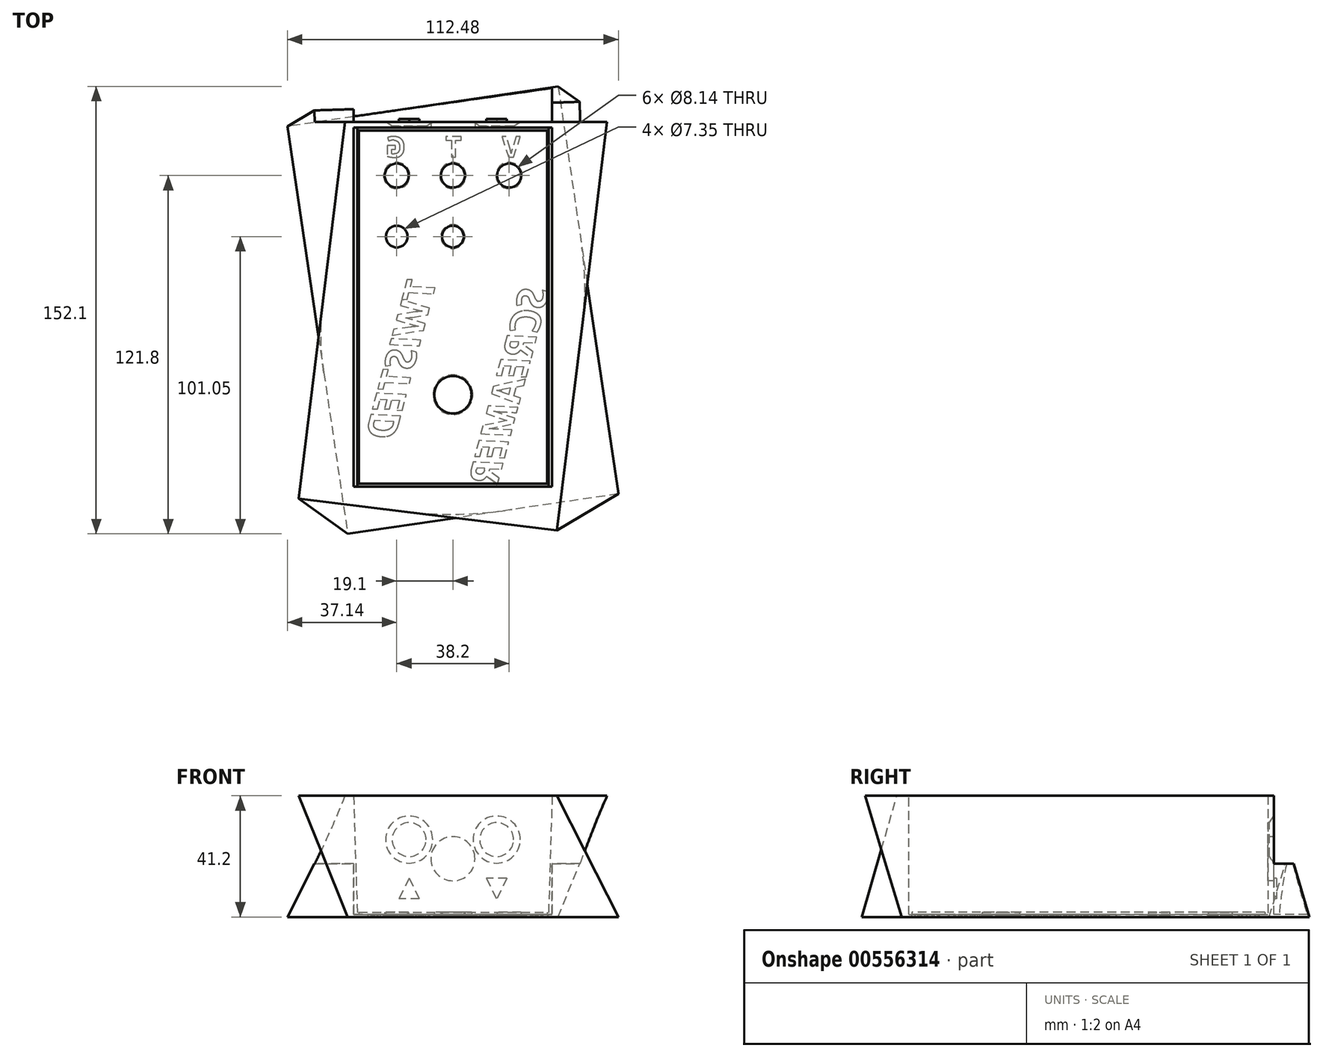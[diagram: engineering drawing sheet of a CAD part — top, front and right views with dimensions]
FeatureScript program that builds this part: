
annotation { "Feature Type Name" : "Feature", "Feature Type Description" : "" }
export const myFeature = defineFeature(function(context is Context, id is Id, definition is map)
    precondition{}
    {
        {
            var Q0;
            Q0=qCreatedBy(makeId("Top.planeOp"),FACE);
            var sketch = newSketch(context, id + "F0", { "sketchPlane" : qUnion([Q0])});
            skLineSegment(sketch, "E0.bottom", {"start": v(-36.5, 64) * mm, "end": v(36.5, 64) * mm});
            skLineSegment(sketch, "E0.top", {"start": v(-36.5, -64) * mm, "end": v(36.5, -64) * mm});
            skLineSegment(sketch, "E0.left", {"start": v(-36.5, 64) * mm, "end": v(-36.5, -64) * mm});
            skLineSegment(sketch, "E0.right", {"start": v(36.5, 64) * mm, "end": v(36.5, -64) * mm});
            skSolve(sketch);
        }
        {
            var Q0;
            Q0=makeQuery(id+"F0.imprint","IMPRINT",FACE,{"disambiguationData":[TD([[makeQuery(id+"F0.imprint","IMPRINT",EDGE,{"derivedFrom":sQuery(id+"F0.wireOp",EDGE,"E0.bottom")}),-1.0]])]});
            extrude(context, id + "F1", {"entities" : qUnion([Q0]), "depth" : 41.2 * mm, "offsetDistance" : 25 * mm});
        }
        {
            var Q0;
            {var subQ0=sQuery(id+"F0.wireOp",EDGE,"E0.bottom");var subQ1=sQuery(id+"F0.wireOp",EDGE,"E0.left");var subQ2=sQuery(id+"F0.wireOp",EDGE,"E0.top");var subQ3=sQuery(id+"F0.wireOp",EDGE,"E0.right");Q0=makeQuery(id+"F16.boolean.opBoolean","SPLIT",FACE,{"disambiguationData":[TD([makeQuery(id+"F1.opExtrude","SWEPT_FACE",FACE,{"disambiguationData":[OSD([subQ0])]})])],"derivedFrom":makeQuery(id+"F1.opExtrude","CAP_FACE",FACE,{"disambiguationData":[OSD([subQ0,subQ2,subQ1,subQ3])],"isStart":true})});}
            var sketch = newSketch(context, id + "F2", { "sketchPlane" : qUnion([Q0])});
            skLineSegment(sketch, "E1.bottom", {"start": v(35.76, -75.05) * mm, "end": v(-56.24, -61.45) * mm});
            skLineSegment(sketch, "E1.top", {"start": v(56.24, 63.45) * mm, "end": v(-35.76, 77.05) * mm});
            skLineSegment(sketch, "E1.left", {"start": v(35.76, -75.05) * mm, "end": v(56.24, 63.45) * mm});
            skLineSegment(sketch, "E1.right", {"start": v(-56.24, -61.45) * mm, "end": v(-35.76, 77.05) * mm});
            skPoint(sketch, "E1.middle", {"position": v(0, 1) * mm});
            skSolve(sketch);
        }
        {
            var Q0;
            Q0=makeQuery(id+"F1.opExtrude","CAP_FACE",FACE,{"disambiguationData":[OSD([sQuery(id+"F0.wireOp",EDGE,"E0.bottom"),sQuery(id+"F0.wireOp",EDGE,"E0.top"),sQuery(id+"F0.wireOp",EDGE,"E0.left"),sQuery(id+"F0.wireOp",EDGE,"E0.right")])],"isStart":false});
            var sketch = newSketch(context, id + "F3", { "sketchPlane" : qUnion([Q0])});
            skLineSegment(sketch, "E2.bottom", {"start": v(-35.35, 73.87) * mm, "end": v(52.41, 63.1) * mm});
            skLineSegment(sketch, "E2.top", {"start": v(-52.41, -65.1) * mm, "end": v(35.35, -75.87) * mm});
            skLineSegment(sketch, "E2.left", {"start": v(-35.35, 73.87) * mm, "end": v(-52.41, -65.1) * mm});
            skLineSegment(sketch, "E2.right", {"start": v(52.41, 63.1) * mm, "end": v(35.35, -75.87) * mm});
            skPoint(sketch, "E2.middle", {"position": v(0, -1) * mm});
            skSolve(sketch);
        }
        {
            var Q1;
            Q1=qSketchRegion(id+"F2",true);
            var Q2;
            Q2=qSketchRegion(id+"F3",true);
            var Q3;
            Q3=sQuery(id+"F2.wireOp",VERTEX,"E1.left.start");
            var Q4;
            Q4=sQuery(id+"F3.wireOp",VERTEX,"E2.right.start");
            loft(context, id + "F4", {"operationType" : NewBodyOperationType.ADD, "sheetProfilesArray" : [{ "sheetProfileEntities" : qUnion([Q1]) }, { "sheetProfileEntities" : qUnion([Q2]) }], "matchConnections" : true, "connections" : [{ "connectionEntities" : qUnion([Q3, Q4]), "connectionEdgeQueries" : qUnion([]), "connectionEdgeParameters" : [] }]});
        }
        {
            var Q0;
            Q0=makeQuery(id+"F1.opExtrude","CAP_FACE",FACE,{"disambiguationData":[OSD([sQuery(id+"F0.wireOp",EDGE,"E0.bottom"),sQuery(id+"F0.wireOp",EDGE,"E0.top"),sQuery(id+"F0.wireOp",EDGE,"E0.left"),sQuery(id+"F0.wireOp",EDGE,"E0.right")])],"isStart":false});
            var sketch = newSketch(context, id + "F5", { "sketchPlane" : qUnion([Q0])});
            skLineSegment(sketch, "E3.bottom", {"start": v(-33.75, 61) * mm, "end": v(33.75, 61) * mm});
            skLineSegment(sketch, "E3.top", {"start": v(-33.75, -61) * mm, "end": v(33.75, -61) * mm});
            skLineSegment(sketch, "E3.left", {"start": v(-33.75, 61) * mm, "end": v(-33.75, -61) * mm});
            skLineSegment(sketch, "E3.right", {"start": v(33.75, 61) * mm, "end": v(33.75, -61) * mm});
            skSolve(sketch);
        }
        {
            var Q0;
            Q0=makeQuery(id+"F5.imprint","IMPRINT",FACE,{"disambiguationData":[TD([[makeQuery(id+"F5.imprint","IMPRINT",EDGE,{"derivedFrom":sQuery(id+"F5.wireOp",EDGE,"E3.bottom")}),-1.0]])]});
            extrude(context, id + "F6", {"entities" : qUnion([Q0]), "operationType" : NewBodyOperationType.REMOVE, "oppositeDirection" : true, "depth" : 40.4 * mm, "offsetDistance" : 25 * mm});
        }
        {
            var Q0;
            Q0=makeQuery(id+"F6.boolean.opBoolean","COPY",FACE,{"derivedFrom":makeQuery(id+"F6.opExtrude","CAP_FACE",FACE,{"disambiguationData":[OSD([sQuery(id+"F5.wireOp",EDGE,"E3.bottom"),sQuery(id+"F5.wireOp",EDGE,"E3.top"),sQuery(id+"F5.wireOp",EDGE,"E3.left"),sQuery(id+"F5.wireOp",EDGE,"E3.right")])],"isStart":false})});
            var sketch = newSketch(context, id + "F7", { "sketchPlane" : qUnion([Q0])});
            skCircle(sketch, "E4", {"center": v(-19.1, 44.75) * mm, "radius": 4.07 * mm});
            skCircle(sketch, "E5", {"center": v(0, 44.75) * mm, "radius": 4.07 * mm});
            skCircle(sketch, "E6", {"center": v(19.1, 44.75) * mm, "radius": 4.07 * mm});
            skCircle(sketch, "E7", {"center": v(0, -29.75) * mm, "radius": 6.35 * mm});
            skLineSegment(sketch, "E8", {"start": v(19.1, 44.75) * mm, "end": v(0, 44.75) * mm, "construction": true});
            skCircle(sketch, "E9", {"center": v(0, 24) * mm, "radius": 3.67 * mm});
            skCircle(sketch, "E10", {"center": v(-19.1, 24) * mm, "radius": 3.67 * mm});
            skSolve(sketch);
        }
        {
            var Q0;
            Q0=qSketchRegion(id+"F7",true);
            extrude(context, id + "F8", {"entities" : qUnion([Q0]), "operationType" : NewBodyOperationType.REMOVE, "oppositeDirection" : true, "depth" : 25 * mm, "offsetDistance" : 25 * mm});
        }
        {
            var Q0;
            Q0=makeQuery(id+"F6.boolean.opBoolean","COPY",FACE,{"derivedFrom":makeQuery(id+"F6.opExtrude","SWEPT_FACE",FACE,{"disambiguationData":[OSD([sQuery(id+"F5.wireOp",EDGE,"E3.bottom")])]})});
            cPlane(context, id + "F9", {"entities" : qUnion([Q0]), "cplaneType" : CPlaneType.OFFSET, "offset" : 2 * mm, "oppositeDirection" : true, "width" : 150 * mm, "height" : 150 * mm});
        }
        {
            var Q0;
            Q0=qCreatedBy(id+"F9.planeOp",FACE);
            var sketch = newSketch(context, id + "F10", { "sketchPlane" : qUnion([Q0])});
            skCircle(sketch, "E11", {"center": v(0, 19.8) * mm, "radius": 7.5 * mm});
            skCircle(sketch, "E12", {"center": v(14.87, 26.3) * mm, "radius": 5.76 * mm});
            skCircle(sketch, "E13", {"center": v(-14.88, 26.3) * mm, "radius": 5.76 * mm});
            skSolve(sketch);
        }
        {
            var Q0;
            Q0=qSketchRegion(id+"F10",true);
            extrude(context, id + "F11", {"entities" : qUnion([Q0]), "operationType" : NewBodyOperationType.REMOVE, "endBound" : BoundingType.SYMMETRIC, "oppositeDirection" : true, "depth" : 30 * mm, "offsetDistance" : 25 * mm});
        }
        {
            var Q0;
            Q0=qCreatedBy(id+"F9.planeOp",FACE);
            var sketch = newSketch(context, id + "F12", { "sketchPlane" : qUnion([Q0])});
            skLineSegment(sketch, "E14.0", {"start": v(-33.75, 0.8) * mm, "end": v(-33.75, 41.2) * mm});
            skLineSegment(sketch, "E15.0", {"start": v(-33.75, 0.8) * mm, "end": v(33.75, 0.8) * mm});
            skLineSegment(sketch, "E16.0", {"start": v(33.75, 0.8) * mm, "end": v(33.75, 41.2) * mm});
            skLineSegment(sketch, "E17.0", {"start": v(-33.75, 41.2) * mm, "end": v(33.75, 41.2) * mm});
            skSolve(sketch);
        }
        {
            var Q0;
            Q0=qSketchRegion(id+"F12",true);
            extrude(context, id + "F13", {"entities" : qUnion([Q0]), "operationType" : NewBodyOperationType.REMOVE, "oppositeDirection" : true, "depth" : 25 * mm, "offsetDistance" : 25 * mm});
        }
        {
            var Q0;
            Q0=qCreatedBy(makeId("Front.planeOp"),FACE);
            cPlane(context, id + "F14", {"entities" : qUnion([Q0]), "cplaneType" : CPlaneType.OFFSET, "offset" : 38 * mm, "width" : 150 * mm, "height" : 150 * mm});
        }
        {
            var Q0;
            Q0=makeQuery(id+"F1.opExtrude","CAP_FACE",FACE,{"disambiguationData":[OSD([sQuery(id+"F0.wireOp",EDGE,"E0.bottom"),sQuery(id+"F0.wireOp",EDGE,"E0.top"),sQuery(id+"F0.wireOp",EDGE,"E0.left"),sQuery(id+"F0.wireOp",EDGE,"E0.right")])],"isStart":true});
            var sketch = newSketch(context, id + "F15", { "sketchPlane" : qUnion([Q0])});
            skText(sketch, "E18", { "text": "V", "fontName": "OpenSans-Bold.ttf"});
            skText(sketch, "E19", { "text": "T", "fontName": "OpenSans-Bold.ttf"});
            skText(sketch, "E20", { "text": "G", "fontName": "OpenSans-Bold.ttf"});
            const initialGuessF15  = {"E18": [0.02295, -0.051, -1, 0, 0.007], "E19": [0.00303, -0.051, -1, 0, 0.007], "E20": [-0.016, -0.051, -1, 0, 0.007]};
            skSetInitialGuess(sketch, initialGuessF15);
            skSolve(sketch);
        }
        {
            var Q0;
            Q0=qSketchRegion(id+"F15",true);
            extrude(context, id + "F16", {"entities" : qUnion([Q0]), "operationType" : NewBodyOperationType.REMOVE, "endBound" : BoundingType.THROUGH_ALL, "oppositeDirection" : true, "depth" : 0.5 * mm, "offsetDistance" : 25 * mm});
        }
        {
            var Q0;
            Q0=makeQuery(id+"F13.boolean.opBoolean","COPY",FACE,{"derivedFrom":makeQuery(id+"F13.opExtrude","CAP_FACE",FACE,{"disambiguationData":[OSD([sQuery(id+"F12.wireOp",EDGE,"E14.0"),sQuery(id+"F12.wireOp",EDGE,"E15.0"),sQuery(id+"F12.wireOp",EDGE,"E16.0"),sQuery(id+"F12.wireOp",EDGE,"E17.0")])],"isStart":true})});
            var sketch = newSketch(context, id + "F17", { "sketchPlane" : qUnion([Q0])});
            skLineSegment(sketch, "E21", {"start": v(75, 18.06) * mm, "end": v(-75, 18.06) * mm});
            skLineSegment(sketch, "E22", {"start": v(-75, 18.06) * mm, "end": v(-75, 44.5) * mm});
            skLineSegment(sketch, "E23", {"start": v(-75, 44.5) * mm, "end": v(75, 44.5) * mm});
            skLineSegment(sketch, "E24", {"start": v(75, 44.5) * mm, "end": v(75, 18.06) * mm});
            skSolve(sketch);
        }
        {
            var Q0;
            Q0=qSketchRegion(id+"F17",true);
            extrude(context, id + "F18", {"entities" : qUnion([Q0]), "operationType" : NewBodyOperationType.REMOVE, "depth" : 15 * mm, "offsetDistance" : 25 * mm});
        }
        {
            var Q0;
            Q0=makeQuery(id+"F13.boolean.opBoolean","INTERSECT",EDGE,{"derivedFrom":[makeQuery(id+"F11.boolean.opBoolean","COPY",FACE,{"derivedFrom":makeQuery(id+"F11.opExtrude","SWEPT_FACE",FACE,{"disambiguationData":[OSD([sQuery(id+"F10.wireOp",EDGE,"E13")])]})}),makeQuery(id+"F13.opExtrude","CAP_FACE",FACE,{"disambiguationData":[OSD([sQuery(id+"F12.wireOp",EDGE,"E14.0"),sQuery(id+"F12.wireOp",EDGE,"E15.0"),sQuery(id+"F12.wireOp",EDGE,"E16.0"),sQuery(id+"F12.wireOp",EDGE,"E17.0")])],"isStart":true})]});
            var Q1;
            Q1=makeQuery(id+"F13.boolean.opBoolean","INTERSECT",EDGE,{"derivedFrom":[makeQuery(id+"F11.boolean.opBoolean","COPY",FACE,{"derivedFrom":makeQuery(id+"F11.opExtrude","SWEPT_FACE",FACE,{"disambiguationData":[OSD([sQuery(id+"F10.wireOp",EDGE,"E12")])]})}),makeQuery(id+"F13.opExtrude","CAP_FACE",FACE,{"disambiguationData":[OSD([sQuery(id+"F12.wireOp",EDGE,"E14.0"),sQuery(id+"F12.wireOp",EDGE,"E15.0"),sQuery(id+"F12.wireOp",EDGE,"E16.0"),sQuery(id+"F12.wireOp",EDGE,"E17.0")])],"isStart":true})]});
            chamfer(context, id + "F19", {"entities" : qUnion([Q0, Q1]), "chamferType" : ChamferType.TWO_OFFSETS, "width1" : 1.5 * mm, "oppositeDirection" : false, "width2" : 2.25 * mm, "tangentPropagation" : true});
        }
        {
            var Q0;
            {var subQ0=sQuery(id+"F0.wireOp",EDGE,"E0.bottom");var subQ1=sQuery(id+"F0.wireOp",EDGE,"E0.top");var subQ2=sQuery(id+"F0.wireOp",EDGE,"E0.left");var subQ3=sQuery(id+"F0.wireOp",EDGE,"E0.right");Q0=makeQuery(id+"F8.boolean.opBoolean","INTERSECT",EDGE,{"derivedFrom":[makeQuery(id+"F4.boolean.opBoolean","MERGE",FACE,{"derivedFrom":[makeQuery(id+"F1.opExtrude","CAP_FACE",FACE,{"disambiguationData":[OSD([subQ0,subQ1,subQ2,subQ3])],"isStart":true}),makeQuery(id+"F4.opLoft","CAP_FACE",FACE,{"disambiguationData":[OSD([makeQuery(id+"F2.imprint","IMPRINT",FACE,{"disambiguationData":[TD([[makeQuery(id+"F2.imprint","IMPRINT",EDGE,{"derivedFrom":makeQuery(id+"F1.opExtrude","CAP_EDGE",EDGE,{"disambiguationData":[OSD([subQ0])],"isStart":true})}),1.0]])]})])],"isStart":true})]}),makeQuery(id+"F8.opExtrude","SWEPT_FACE",FACE,{"disambiguationData":[OSD([sQuery(id+"F7.wireOp",EDGE,"E6")])]})]});}
            var Q1;
            {var subQ0=sQuery(id+"F0.wireOp",EDGE,"E0.bottom");var subQ1=sQuery(id+"F0.wireOp",EDGE,"E0.top");var subQ2=sQuery(id+"F0.wireOp",EDGE,"E0.left");var subQ3=sQuery(id+"F0.wireOp",EDGE,"E0.right");Q1=makeQuery(id+"F8.boolean.opBoolean","INTERSECT",EDGE,{"derivedFrom":[makeQuery(id+"F4.boolean.opBoolean","MERGE",FACE,{"derivedFrom":[makeQuery(id+"F1.opExtrude","CAP_FACE",FACE,{"disambiguationData":[OSD([subQ0,subQ1,subQ2,subQ3])],"isStart":true}),makeQuery(id+"F4.opLoft","CAP_FACE",FACE,{"disambiguationData":[OSD([makeQuery(id+"F2.imprint","IMPRINT",FACE,{"disambiguationData":[TD([[makeQuery(id+"F2.imprint","IMPRINT",EDGE,{"derivedFrom":makeQuery(id+"F1.opExtrude","CAP_EDGE",EDGE,{"disambiguationData":[OSD([subQ0])],"isStart":true})}),1.0]])]})])],"isStart":true})]}),makeQuery(id+"F8.opExtrude","SWEPT_FACE",FACE,{"disambiguationData":[OSD([sQuery(id+"F7.wireOp",EDGE,"E5")])]})]});}
            var Q2;
            {var subQ0=sQuery(id+"F0.wireOp",EDGE,"E0.bottom");var subQ1=sQuery(id+"F0.wireOp",EDGE,"E0.top");var subQ2=sQuery(id+"F0.wireOp",EDGE,"E0.left");var subQ3=sQuery(id+"F0.wireOp",EDGE,"E0.right");Q2=makeQuery(id+"F8.boolean.opBoolean","INTERSECT",EDGE,{"derivedFrom":[makeQuery(id+"F4.boolean.opBoolean","MERGE",FACE,{"derivedFrom":[makeQuery(id+"F1.opExtrude","CAP_FACE",FACE,{"disambiguationData":[OSD([subQ0,subQ1,subQ2,subQ3])],"isStart":true}),makeQuery(id+"F4.opLoft","CAP_FACE",FACE,{"disambiguationData":[OSD([makeQuery(id+"F2.imprint","IMPRINT",FACE,{"disambiguationData":[TD([[makeQuery(id+"F2.imprint","IMPRINT",EDGE,{"derivedFrom":makeQuery(id+"F1.opExtrude","CAP_EDGE",EDGE,{"disambiguationData":[OSD([subQ0])],"isStart":true})}),1.0]])]})])],"isStart":true})]}),makeQuery(id+"F8.opExtrude","SWEPT_FACE",FACE,{"disambiguationData":[OSD([sQuery(id+"F7.wireOp",EDGE,"E4")])]})]});}
            var Q3;
            {var subQ0=sQuery(id+"F0.wireOp",EDGE,"E0.bottom");var subQ1=sQuery(id+"F0.wireOp",EDGE,"E0.top");var subQ2=sQuery(id+"F0.wireOp",EDGE,"E0.left");var subQ3=sQuery(id+"F0.wireOp",EDGE,"E0.right");Q3=makeQuery(id+"F8.boolean.opBoolean","INTERSECT",EDGE,{"derivedFrom":[makeQuery(id+"F4.boolean.opBoolean","MERGE",FACE,{"derivedFrom":[makeQuery(id+"F1.opExtrude","CAP_FACE",FACE,{"disambiguationData":[OSD([subQ0,subQ1,subQ2,subQ3])],"isStart":true}),makeQuery(id+"F4.opLoft","CAP_FACE",FACE,{"disambiguationData":[OSD([makeQuery(id+"F2.imprint","IMPRINT",FACE,{"disambiguationData":[TD([[makeQuery(id+"F2.imprint","IMPRINT",EDGE,{"derivedFrom":makeQuery(id+"F1.opExtrude","CAP_EDGE",EDGE,{"disambiguationData":[OSD([subQ0])],"isStart":true})}),1.0]])]})])],"isStart":true})]}),makeQuery(id+"F8.opExtrude","SWEPT_FACE",FACE,{"disambiguationData":[OSD([sQuery(id+"F7.wireOp",EDGE,"E9")])]})]});}
            var Q4;
            {var subQ0=sQuery(id+"F0.wireOp",EDGE,"E0.bottom");var subQ1=sQuery(id+"F0.wireOp",EDGE,"E0.top");var subQ2=sQuery(id+"F0.wireOp",EDGE,"E0.left");var subQ3=sQuery(id+"F0.wireOp",EDGE,"E0.right");Q4=makeQuery(id+"F8.boolean.opBoolean","INTERSECT",EDGE,{"derivedFrom":[makeQuery(id+"F4.boolean.opBoolean","MERGE",FACE,{"derivedFrom":[makeQuery(id+"F1.opExtrude","CAP_FACE",FACE,{"disambiguationData":[OSD([subQ0,subQ1,subQ2,subQ3])],"isStart":true}),makeQuery(id+"F4.opLoft","CAP_FACE",FACE,{"disambiguationData":[OSD([makeQuery(id+"F2.imprint","IMPRINT",FACE,{"disambiguationData":[TD([[makeQuery(id+"F2.imprint","IMPRINT",EDGE,{"derivedFrom":makeQuery(id+"F1.opExtrude","CAP_EDGE",EDGE,{"disambiguationData":[OSD([subQ0])],"isStart":true})}),1.0]])]})])],"isStart":true})]}),makeQuery(id+"F8.opExtrude","SWEPT_FACE",FACE,{"disambiguationData":[OSD([sQuery(id+"F7.wireOp",EDGE,"KNiFqmuv-MMCi-B5FO-T3GH-z67XstVQp584")])]})]});}
            var Q5;
            {var subQ0=sQuery(id+"F0.wireOp",EDGE,"E0.bottom");var subQ1=sQuery(id+"F0.wireOp",EDGE,"E0.top");var subQ2=sQuery(id+"F0.wireOp",EDGE,"E0.left");var subQ3=sQuery(id+"F0.wireOp",EDGE,"E0.right");Q5=makeQuery(id+"F8.boolean.opBoolean","INTERSECT",EDGE,{"derivedFrom":[makeQuery(id+"F4.boolean.opBoolean","MERGE",FACE,{"derivedFrom":[makeQuery(id+"F1.opExtrude","CAP_FACE",FACE,{"disambiguationData":[OSD([subQ0,subQ1,subQ2,subQ3])],"isStart":true}),makeQuery(id+"F4.opLoft","CAP_FACE",FACE,{"disambiguationData":[OSD([makeQuery(id+"F2.imprint","IMPRINT",FACE,{"disambiguationData":[TD([[makeQuery(id+"F2.imprint","IMPRINT",EDGE,{"derivedFrom":makeQuery(id+"F1.opExtrude","CAP_EDGE",EDGE,{"disambiguationData":[OSD([subQ0])],"isStart":true})}),1.0]])]})])],"isStart":true})]}),makeQuery(id+"F8.opExtrude","SWEPT_FACE",FACE,{"disambiguationData":[OSD([sQuery(id+"F7.wireOp",EDGE,"E7")])]})]});}
            chamfer(context, id + "F20", {"entities" : qUnion([Q0, Q1, Q2, Q3, Q4, Q5]), "width" : 0.4 * mm, "tangentPropagation" : true});
        }
        {
            var Q0;
            {var subQ0=sQuery(id+"F0.wireOp",EDGE,"E0.bottom");var subQ1=sQuery(id+"F0.wireOp",EDGE,"E0.top");var subQ2=sQuery(id+"F0.wireOp",EDGE,"E0.left");var subQ3=sQuery(id+"F0.wireOp",EDGE,"E0.right");Q0=makeQuery(id+"F4.boolean.opBoolean","MERGE",FACE,{"derivedFrom":[makeQuery(id+"F1.opExtrude","CAP_FACE",FACE,{"disambiguationData":[OSD([subQ0,subQ1,subQ2,subQ3])],"isStart":true}),makeQuery(id+"F4.opLoft","CAP_FACE",FACE,{"disambiguationData":[OSD([makeQuery(id+"F2.imprint","IMPRINT",FACE,{"disambiguationData":[TD([[makeQuery(id+"F2.imprint","IMPRINT",EDGE,{"derivedFrom":makeQuery(id+"F1.opExtrude","CAP_EDGE",EDGE,{"disambiguationData":[OSD([subQ0])],"isStart":true})}),1.0]])]})])],"isStart":true})]});}
            var sketch = newSketch(context, id + "F21", { "sketchPlane" : qUnion([Q0])});
            skText(sketch, "E25", { "text": "  TWISTED\n\nSCREAMER", "fontName": "OpenSans-BoldItalic.ttf"});
            const initialGuessF21  = {"E25": [-0.00375, -0.01526, -0.25882, 0.96593, 0.01]};
            skSetInitialGuess(sketch, initialGuessF21);
            skSolve(sketch);
        }
        {
            var Q0;
            Q0=qSketchRegion(id+"F21",true);
            extrude(context, id + "F22", {"entities" : qUnion([Q0]), "operationType" : NewBodyOperationType.REMOVE, "endBound" : BoundingType.THROUGH_ALL, "oppositeDirection" : true, "depth" : 25 * mm, "offsetDistance" : 25 * mm});
        }
        {
            var Q0;
            Q0=makeQuery(id+"F18.boolean.opBoolean","MERGE",FACE,{"derivedFrom":[makeQuery(id+"F13.boolean.opBoolean","COPY",FACE,{"derivedFrom":makeQuery(id+"F13.opExtrude","CAP_FACE",FACE,{"disambiguationData":[OSD([sQuery(id+"F12.wireOp",EDGE,"E14.0"),sQuery(id+"F12.wireOp",EDGE,"E15.0"),sQuery(id+"F12.wireOp",EDGE,"E16.0"),sQuery(id+"F12.wireOp",EDGE,"E17.0")])],"isStart":true})}),makeQuery(id+"F18.opExtrude","CAP_FACE",FACE,{"disambiguationData":[OSD([sQuery(id+"F17.wireOp",EDGE,"E21"),sQuery(id+"F17.wireOp",EDGE,"E22"),sQuery(id+"F17.wireOp",EDGE,"E23"),sQuery(id+"F17.wireOp",EDGE,"E24")])],"isStart":true})]});
            var sketch = newSketch(context, id + "F23", { "sketchPlane" : qUnion([Q0])});
            skLineSegment(sketch, "E26", {"start": v(14.88, 26.3) * mm, "end": v(14.88, 6.07) * mm, "construction": true});
            skLineSegment(sketch, "E27", {"start": v(-14.87, 26.3) * mm, "end": v(-14.87, 6.07) * mm, "construction": true});
            skLineSegment(sketch, "E28", {"start": v(-18.37, 13.12) * mm, "end": v(-14.87, 13.12) * mm});
            skLineSegment(sketch, "E29", {"start": v(-18.37, 13.12) * mm, "end": v(-14.87, 6.12) * mm});
            skLineSegment(sketch, "E30", {"start": v(14.88, 13.12) * mm, "end": v(18.38, 6.12) * mm});
            skLineSegment(sketch, "E31", {"start": v(18.38, 6.12) * mm, "end": v(14.88, 6.12) * mm});
            skLineSegment(sketch, "E32.MirrorCS", {"start": v(11.38, 6.12) * mm, "end": v(14.88, 6.12) * mm});
            skLineSegment(sketch, "E33.MirrorCS", {"start": v(14.88, 13.12) * mm, "end": v(11.38, 6.12) * mm});
            skLineSegment(sketch, "E34.MirrorCS", {"start": v(-11.37, 13.12) * mm, "end": v(-14.87, 6.12) * mm});
            skLineSegment(sketch, "E35.MirrorCS", {"start": v(-11.37, 13.12) * mm, "end": v(-14.87, 13.12) * mm});
            skSolve(sketch);
        }
        {
            var Q0;
            Q0 = qSketchRegion(id + "F23", true);
            extrude(context, id + "F24", {"entities" : qUnion([Q0]), "operationType" : NewBodyOperationType.ADD, "depth" : 1 * mm, "offsetDistance" : 25 * mm});
        }
        {
            var Q0;
            {var subQ0=sQuery(id+"F5.wireOp",EDGE,"E3.bottom");var subQ1=sQuery(id+"F5.wireOp",EDGE,"E3.left");var subQ2=sQuery(id+"F5.wireOp",EDGE,"E3.top");var subQ3=sQuery(id+"F5.wireOp",EDGE,"E3.right");Q0=makeQuery(id+"F22.boolean.opBoolean","SPLIT",FACE,{"disambiguationData":[TD([makeQuery(id+"F6.boolean.opBoolean","COPY",FACE,{"derivedFrom":makeQuery(id+"F6.opExtrude","SWEPT_FACE",FACE,{"disambiguationData":[OSD([subQ0])]})})])],"derivedFrom":makeQuery(id+"F6.boolean.opBoolean","COPY",FACE,{"derivedFrom":makeQuery(id+"F6.opExtrude","CAP_FACE",FACE,{"disambiguationData":[OSD([subQ0,subQ2,subQ1,subQ3])],"isStart":false})})});}
            var sketch = newSketch(context, id + "F25", { "sketchPlane" : qUnion([Q0])});
            skLineSegment(sketch, "E36.bottom", {"start": v(-32, 60) * mm, "end": v(32, 60) * mm});
            skLineSegment(sketch, "E36.top", {"start": v(2.3, -60) * mm, "end": v(17.26, -60) * mm});
            skLineSegment(sketch, "E36.left", {"start": v(-32, 60) * mm, "end": v(-32, 11.66) * mm});
            skLineSegment(sketch, "E36.right", {"start": v(32, 60) * mm, "end": v(32, -5) * mm});
            skPoint(sketch, "E36.middle", {"position": v(0, 0) * mm});
            skCircle(sketch, "E37.0", {"center": v(-19.1, 44.75) * mm, "radius": 4.07 * mm});
            skCircle(sketch, "E38.0", {"center": v(0, 44.75) * mm, "radius": 4.07 * mm});
            skCircle(sketch, "E39.0", {"center": v(19.1, 44.75) * mm, "radius": 4.07 * mm});
            skCircle(sketch, "E40.0", {"center": v(0, 24) * mm, "radius": 3.67 * mm});
            skCircle(sketch, "E41.0", {"center": v(-19.1, 24) * mm, "radius": 3.68 * mm});
            skCircle(sketch, "E42.0", {"center": v(0, -29.75) * mm, "radius": 6.35 * mm});
            skPoint(sketch, "E43.orphan", {"position": v(-32, -60) * mm});
            skLineSegment(sketch, "E44", {"start": v(17.26, -60) * mm, "end": v(32, -5) * mm});
            skPoint(sketch, "E45.orphan", {"position": v(32, -60) * mm});
            skLineSegment(sketch, "E46", {"start": v(-32, -44.12) * mm, "end": v(-32, -46.92) * mm});
            skLineSegment(sketch, "E47", {"start": v(-32, 11.66) * mm, "end": v(-32, -44.12) * mm});
            skLineSegment(sketch, "E48", {"start": v(-32, -46.92) * mm, "end": v(-32, -60) * mm});
            skLineSegment(sketch, "E49", {"start": v(-32, -60) * mm, "end": v(2.3, -60) * mm});
            skLineSegment(sketch, "E50", {"start": v(17.26, -60) * mm, "end": v(32, -60) * mm});
            skLineSegment(sketch, "E51", {"start": v(32, -5) * mm, "end": v(32, -60) * mm});
            skPoint(sketch, "E52.7.internal.orphan", {"position": v(16.25, 0) * mm});
            skSolve(sketch);
        }
        {
            var Q0;
            Q0 = qSketchRegion(id + "F25", true);
            extrude(context, id + "F26", {"entities" : qUnion([Q0]), "depth" : 0.8 * mm, "offsetDistance" : 25 * mm});
        }
        {
            var Q0;
            Q0=makeQuery(id+"F6.boolean.opBoolean","COPY",EDGE,{"derivedFrom":makeQuery(id+"F6.opExtrude","CAP_EDGE",EDGE,{"disambiguationData":[OSD([sQuery(id+"F5.wireOp",EDGE,"E3.left")])],"isStart":false})});
            var Q1;
            Q1=makeQuery(id+"F6.boolean.opBoolean","COPY",EDGE,{"derivedFrom":makeQuery(id+"F6.opExtrude","CAP_EDGE",EDGE,{"disambiguationData":[OSD([sQuery(id+"F5.wireOp",EDGE,"E3.right")])],"isStart":false})});
            chamfer(context, id + "F27", {"entities" : qUnion([Q0, Q1]), "chamferType" : ChamferType.TWO_OFFSETS, "width1" : 1.25 * mm, "oppositeDirection" : false, "width2" : 40.4 * mm, "tangentPropagation" : true});
        }
    });
